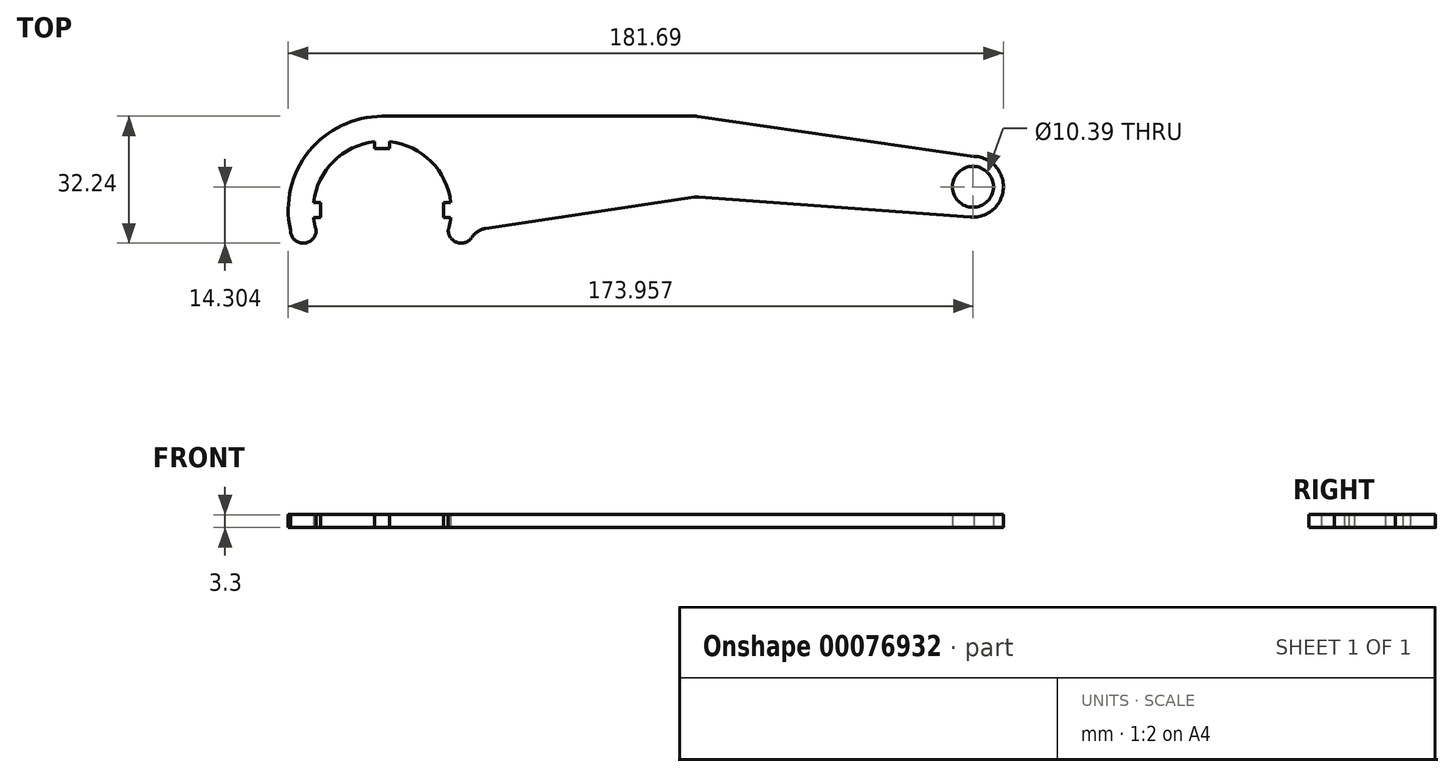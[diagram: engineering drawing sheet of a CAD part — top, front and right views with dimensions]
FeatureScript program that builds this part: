
annotation { "Feature Type Name" : "Feature", "Feature Type Description" : "" }
export const myFeature = defineFeature(function(context is Context, id is Id, definition is map)
    precondition{}
    {
        {
            var Q0;
            Q0=qCreatedBy(makeId("Top.planeOp"),FACE);
            var sketch = newSketch(context, id + "F0", { "sketchPlane" : qUnion([Q0])});
            skCircle(sketch, "E0", {"center": v(0, 0) * mm, "radius": 17.53 * mm, "construction": true});
            skCircle(sketch, "E1", {"center": v(0, 0) * mm, "radius": 23.88 * mm, "construction": true});
            skArc(sketch, "E2", {"start": v(16.77, -5.08) * mm, "mid": v(0, 17.53) * mm, "end": v(-16.77, -5.08) * mm});
            skLineSegment(sketch, "E3", {"start": v(-17.53, 0) * mm, "end": v(-15.62, 0) * mm, "construction": true});
            skLineSegment(sketch, "E4.bottom", {"start": v(-17.42, 1.9) * mm, "end": v(-15.62, 1.9) * mm});
            skLineSegment(sketch, "E4.top", {"start": v(-17.42, -1.9) * mm, "end": v(-15.62, -1.9) * mm});
            skLineSegment(sketch, "E4.right", {"start": v(-15.62, 1.9) * mm, "end": v(-15.62, -1.9) * mm});
            skLineSegment(sketch, "E5", {"start": v(0, 17.53) * mm, "end": v(0, 15.62) * mm, "construction": true});
            skPoint(sketch, "E5.endSnap0", {"position": v(0, 17.53) * mm});
            skLineSegment(sketch, "E6.top", {"start": v(-1.9, 15.62) * mm, "end": v(1.9, 15.62) * mm});
            skLineSegment(sketch, "E6.left", {"start": v(-1.9, 17.42) * mm, "end": v(-1.9, 15.62) * mm});
            skLineSegment(sketch, "E6.right", {"start": v(1.9, 17.42) * mm, "end": v(1.9, 15.62) * mm});
            skLineSegment(sketch, "E7", {"start": v(17.53, 0) * mm, "end": v(15.62, 0) * mm, "construction": true});
            skLineSegment(sketch, "E8.bottom", {"start": v(15.62, 1.9) * mm, "end": v(17.42, 1.9) * mm});
            skLineSegment(sketch, "E8.top", {"start": v(15.62, -1.9) * mm, "end": v(17.42, -1.9) * mm});
            skLineSegment(sketch, "E8.left", {"start": v(15.62, 1.9) * mm, "end": v(15.62, -1.9) * mm});
            skLineSegment(sketch, "E9", {"start": v(16.77, -5.08) * mm, "end": v(23.33, -5.08) * mm, "construction": true});
            skLineSegment(sketch, "E10", {"start": v(-16.77, -5.08) * mm, "end": v(-23.33, -5.08) * mm, "construction": true});
            skLineSegment(sketch, "E11", {"start": v(23.33, -5.08) * mm, "end": v(79.85, 3.4) * mm});
            skLineSegment(sketch, "E12", {"start": v(79.85, 3.4) * mm, "end": v(149.5, -1.77) * mm});
            skLineSegment(sketch, "E13", {"start": v(0, 23.88) * mm, "end": v(79.85, 23.88) * mm});
            skLineSegment(sketch, "E14", {"start": v(79.85, 23.88) * mm, "end": v(150.32, 13.68) * mm});
            skLineSegment(sketch, "E15", {"start": v(79.85, 23.88) * mm, "end": v(79.85, 3.4) * mm, "construction": true});
            skArc(sketch, "E16", {"start": v(0, 23.88) * mm, "mid": v(-18.6, 14.98) * mm, "end": v(-23.33, -5.08) * mm});
            skArc(sketch, "E17", {"start": v(149.5, -1.77) * mm, "mid": v(157.8, 5.54) * mm, "end": v(150.32, 13.68) * mm});
            skArc(sketch, "E18", {"start": v(-23.33, -5.08) * mm, "mid": v(-20.05, -8.36) * mm, "end": v(-16.77, -5.08) * mm});
            skArc(sketch, "E19", {"start": v(16.77, -5.08) * mm, "mid": v(20.05, -8.36) * mm, "end": v(23.33, -5.08) * mm});
            skCircle(sketch, "E20", {"center": v(150.08, 5.94) * mm, "radius": 5.2 * mm});
            skSolve(sketch);
        }
        {
            var Q0;
            Q0=makeQuery(id+"F0.imprint","IMPRINT",FACE,{"disambiguationData":[TD([[makeQuery(id+"F0.imprint","IMPRINT",EDGE,{"derivedFrom":sQuery(id+"F0.wireOp",EDGE,"E11")}),1.0]])]});
            var Q1;
            Q1=makeQuery(id+"F0.imprint","IMPRINT",FACE,{"disambiguationData":[TD([[makeQuery(id+"F0.imprint","IMPRINT",EDGE,{"derivedFrom":sQuery(id+"F0.wireOp",EDGE,"E6.top")}),1.0]])]});
            var Q2;
            {var subQ0=sQuery(id+"F0.wireOp",EDGE,"E8.bottom");Q2=makeQuery(id+"F0.imprint","IMPRINT",FACE,{"disambiguationData":[TD([[makeQuery(id+"F0.imprint","IMPRINT",EDGE,{"derivedFrom":subQ0}),-1.0]])]});}
            var Q3;
            {var subQ0=sQuery(id+"F0.wireOp",EDGE,"E4.bottom");Q3=makeQuery(id+"F0.imprint","IMPRINT",FACE,{"disambiguationData":[TD([[makeQuery(id+"F0.imprint","IMPRINT",EDGE,{"derivedFrom":subQ0}),-1.0]])]});}
            extrude(context, id + "F1", {"entities" : qUnion([Q0, Q1, Q2, Q3]), "depth" : 3.3 * mm});
        }
        {
            var Q0;
            Q0=makeQuery(id+"F1.opExtrude","SWEPT_EDGE",EDGE,{"disambiguationData":[OSD([sQuery(id+"F0.wireOp",EDGE,"E11"),sQuery(id+"F0.wireOp",EDGE,"E19")])]});
            var Q1;
            Q1=makeQuery(id+"F1.opExtrude","SWEPT_EDGE",EDGE,{"disambiguationData":[OSD([sQuery(id+"F0.wireOp",EDGE,"E11"),sQuery(id+"F0.wireOp",EDGE,"E12")])]});
            var Q2;
            Q2=makeQuery(id+"F1.opExtrude","SWEPT_EDGE",EDGE,{"disambiguationData":[OSD([sQuery(id+"F0.wireOp",EDGE,"E13"),sQuery(id+"F0.wireOp",EDGE,"E14")])]});
            fillet(context, id + "F2", {"entities" : qUnion([Q0, Q1, Q2]), "radius" : 5.08 * mm, "tangentPropagation" : true, "allowEdgeOverflow" : false});
        }
    });
